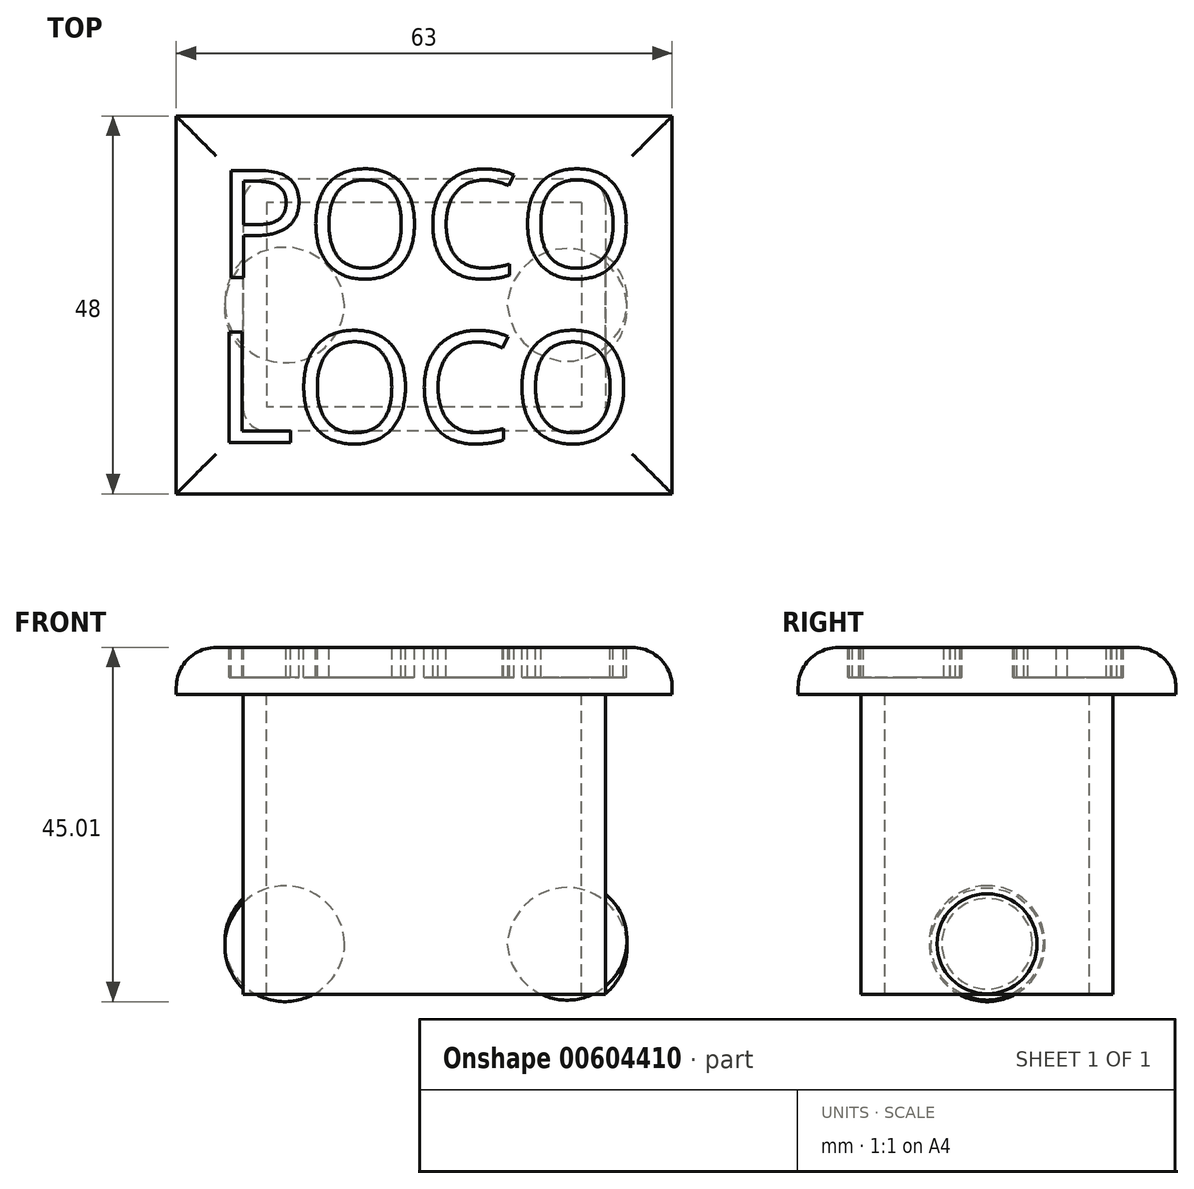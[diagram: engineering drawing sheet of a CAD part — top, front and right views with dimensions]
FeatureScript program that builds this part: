
annotation { "Feature Type Name" : "Feature", "Feature Type Description" : "" }
export const myFeature = defineFeature(function(context is Context, id is Id, definition is map)
    precondition{}
    {
        {
            var Q0;
            Q0=qCreatedBy(makeId("Top.planeOp"),FACE);
            var sketch = newSketch(context, id + "F0", { "sketchPlane" : qUnion([Q0])});
            skLineSegment(sketch, "E0.bottom", {"start": v(31.5, -24) * mm, "end": v(-31.5, -24) * mm});
            skLineSegment(sketch, "E0.top", {"start": v(31.5, 24) * mm, "end": v(-31.5, 24) * mm});
            skLineSegment(sketch, "E0.left", {"start": v(31.5, -24) * mm, "end": v(31.5, 24) * mm});
            skLineSegment(sketch, "E0.right", {"start": v(-31.5, -24) * mm, "end": v(-31.5, 24) * mm});
            skPoint(sketch, "E0.middle", {"position": v(0, 0) * mm});
            skSolve(sketch);
        }
        {
            var Q0;
            Q0=makeQuery(id+"F0.imprint","IMPRINT",FACE,{"disambiguationData":[TD([[makeQuery(id+"F0.imprint","IMPRINT",EDGE,{"derivedFrom":sQuery(id+"F0.wireOp",EDGE,"E0.bottom")}),-1.0]])]});
            extrude(context, id + "F1", {"entities" : qUnion([Q0]), "depth" : 6 * mm, "offsetDistance" : 25.4 * mm});
        }
        {
            var Q0;
            Q0=makeQuery(id+"F1.opExtrude","CAP_FACE",FACE,{"disambiguationData":[OSD([sQuery(id+"F0.wireOp",EDGE,"E0.bottom"),sQuery(id+"F0.wireOp",EDGE,"E0.top"),sQuery(id+"F0.wireOp",EDGE,"E0.left"),sQuery(id+"F0.wireOp",EDGE,"E0.right")])],"isStart":true});
            var sketch = newSketch(context, id + "F2", { "sketchPlane" : qUnion([Q0])});
            skLineSegment(sketch, "E1.bottom", {"start": v(20, -16) * mm, "end": v(-20, -16) * mm});
            skLineSegment(sketch, "E1.top", {"start": v(20, 16) * mm, "end": v(-20, 16) * mm});
            skLineSegment(sketch, "E1.left", {"start": v(23, -13) * mm, "end": v(23, -6.14) * mm});
            skLineSegment(sketch, "E1.right", {"start": v(-23, -13) * mm, "end": v(-23, -5.27) * mm});
            skPoint(sketch, "E1.middle", {"position": v(0, 0) * mm});
            skLineSegment(sketch, "E2.bottom", {"start": v(20, -13) * mm, "end": v(-20, -13) * mm});
            skLineSegment(sketch, "E2.top", {"start": v(20, 13) * mm, "end": v(-20, 13) * mm});
            skLineSegment(sketch, "E2.left", {"start": v(20, -13) * mm, "end": v(20, -6.14) * mm});
            skLineSegment(sketch, "E2.right", {"start": v(-20, -13) * mm, "end": v(-20, -5.27) * mm});
            skPoint(sketch, "E3.visualSharp", {"position": v(-23, 16) * mm});
            skArc(sketch, "E3.filletArc", {"start": v(-20, 16) * mm, "mid": v(-22.12, 15.12) * mm, "end": v(-23, 13) * mm});
            skPoint(sketch, "E4.visualSharp", {"position": v(23, 16) * mm});
            skArc(sketch, "E4.filletArc", {"start": v(23, 13) * mm, "mid": v(22.12, 15.12) * mm, "end": v(20, 16) * mm});
            skPoint(sketch, "E5.visualSharp", {"position": v(23, -16) * mm});
            skArc(sketch, "E5.filletArc", {"start": v(20, -16) * mm, "mid": v(22.12, -15.12) * mm, "end": v(23, -13) * mm});
            skPoint(sketch, "E6.visualSharp", {"position": v(-23, -16) * mm});
            skArc(sketch, "E6.filletArc", {"start": v(-23, -13) * mm, "mid": v(-22.12, -15.12) * mm, "end": v(-20, -16) * mm});
            skLineSegment(sketch, "E7.trimOffspring", {"start": v(-23, -4.17) * mm, "end": v(-23, 4.46) * mm});
            skLineSegment(sketch, "E8.trimOffspring", {"start": v(-20, -4.17) * mm, "end": v(-20, 4.46) * mm});
            skLineSegment(sketch, "E9.trimOffspring", {"start": v(-20, 5.41) * mm, "end": v(-20, 13) * mm});
            skLineSegment(sketch, "E10.trimOffspring", {"start": v(-23, 5.41) * mm, "end": v(-23, 13) * mm});
            skLineSegment(sketch, "E11.trimOffspring", {"start": v(20, 5.32) * mm, "end": v(20, 13) * mm});
            skLineSegment(sketch, "E12.trimOffspring", {"start": v(23, 5.32) * mm, "end": v(23, 13) * mm});
            skLineSegment(sketch, "E13.trimOffspring", {"start": v(20, -4.92) * mm, "end": v(20, 4.27) * mm});
            skLineSegment(sketch, "E14", {"start": v(23, 4.27) * mm, "end": v(23, -4.92) * mm});
            skLineSegment(sketch, "E15", {"start": v(-23, 5.41) * mm, "end": v(-23, 4.46) * mm});
            skLineSegment(sketch, "E16", {"start": v(-23, -5.27) * mm, "end": v(-23, -4.17) * mm});
            skLineSegment(sketch, "E17", {"start": v(-20, -4.17) * mm, "end": v(-20, -5.27) * mm});
            skLineSegment(sketch, "E18", {"start": v(-20, 4.46) * mm, "end": v(-20, 5.41) * mm});
            skLineSegment(sketch, "E19", {"start": v(20, 5.32) * mm, "end": v(20, 4.27) * mm});
            skLineSegment(sketch, "E20", {"start": v(20, -4.92) * mm, "end": v(20, -6.14) * mm});
            skLineSegment(sketch, "E21", {"start": v(23, -6.14) * mm, "end": v(23, -4.92) * mm});
            skLineSegment(sketch, "E22", {"start": v(23, 5.32) * mm, "end": v(23, 4.27) * mm});
            skSolve(sketch);
        }
        {
            var Q0;
            Q0=makeQuery(id+"F2.imprint","IMPRINT",FACE,{"disambiguationData":[TD([[makeQuery(id+"F2.imprint","IMPRINT",EDGE,{"derivedFrom":sQuery(id+"F2.wireOp",EDGE,"E1.bottom")}),-1.0]])]});
            extrude(context, id + "F3", {"entities" : qUnion([Q0]), "operationType" : NewBodyOperationType.ADD, "depth" : 38.1 * mm, "offsetDistance" : 25.4 * mm});
        }
        {
            var Q0;
            Q0=makeQuery(id+"F1.opExtrude","CAP_EDGE",EDGE,{"disambiguationData":[OSD([sQuery(id+"F0.wireOp",EDGE,"E0.right")])],"isStart":false});
            var Q1;
            Q1=makeQuery(id+"F1.opExtrude","CAP_EDGE",EDGE,{"disambiguationData":[OSD([sQuery(id+"F0.wireOp",EDGE,"E0.top")])],"isStart":false});
            var Q2;
            Q2=makeQuery(id+"F1.opExtrude","CAP_EDGE",EDGE,{"disambiguationData":[OSD([sQuery(id+"F0.wireOp",EDGE,"E0.left")])],"isStart":false});
            var Q3;
            Q3=makeQuery(id+"F1.opExtrude","CAP_EDGE",EDGE,{"disambiguationData":[OSD([sQuery(id+"F0.wireOp",EDGE,"E0.bottom")])],"isStart":false});
            fillet(context, id + "F4", {"entities" : qUnion([Q0, Q1, Q2, Q3]), "radius" : 5.08 * mm, "tangentPropagation" : true, "allowEdgeOverflow" : false});
        }
        {
            var Q0;
            Q0=makeQuery(id+"F1.opExtrude","CAP_FACE",FACE,{"disambiguationData":[OSD([sQuery(id+"F0.wireOp",EDGE,"E0.bottom"),sQuery(id+"F0.wireOp",EDGE,"E0.top"),sQuery(id+"F0.wireOp",EDGE,"E0.left"),sQuery(id+"F0.wireOp",EDGE,"E0.right")])],"isStart":false});
            var sketch = newSketch(context, id + "F5", { "sketchPlane" : qUnion([Q0])});
            skText(sketch, "E23", { "text": "POCO", "fontName": "OpenSans-Regular.ttf"});
            skText(sketch, "E24", { "text": "LOCO", "fontName": "OpenSans-Regular.ttf"});
            const initialGuessF5  = {"E23": [-0.02642, 0.00346, 1, 0, 0.01374], "E24": [-0.02671, -0.01748, 1, 0, 0.01416]};
            skSetInitialGuess(sketch, initialGuessF5);
            skSolve(sketch);
        }
        {
            var Q0;
            Q0 = qSketchRegion(id + "F5", true);
            extrude(context, id + "F6", {"entities" : qUnion([Q0]), "operationType" : NewBodyOperationType.REMOVE, "oppositeDirection" : true, "depth" : 3.8 * mm, "offsetDistance" : 25.4 * mm});
        }
        {
            var Q0;
            Q0 = qSketchRegion(id + "F2", true);
            extrude(context, id + "F7", {"entities" : qUnion([Q0]), "operationType" : NewBodyOperationType.ADD, "depth" : 25.4 * mm, "offsetDistance" : 25.4 * mm});
        }
        {
            var Q0;
            Q0=qCreatedBy(makeId("Front.planeOp"),FACE);
            var sketch = newSketch(context, id + "F8", { "sketchPlane" : qUnion([Q0])});
            skLineSegment(sketch, "E25", {"start": v(-23, -37.4) * mm, "end": v(-23, -31.65) * mm});
            skLineSegment(sketch, "E26", {"start": v(-23, -31.65) * mm, "end": v(-25.32, -31.65) * mm});
            skArc(sketch, "E27", {"start": v(-25.32, -31.65) * mm, "mid": v(-24.77, -34.77) * mm, "end": v(-23, -37.4) * mm});
            skSolve(sketch);
        }
        {
            var Q0;
            Q0=makeQuery(id+"F8.imprint","IMPRINT",FACE,{"disambiguationData":[TD([[makeQuery(id+"F8.imprint","IMPRINT",EDGE,{"derivedFrom":sQuery(id+"F8.wireOp",EDGE,"E25")}),1.0]])]});
            var Q1;
            Q1 = qSketchRegion(id + "F8", true);
            var Q2;
            Q2=sQuery(id+"F8.wireOp",EDGE,"E26");
            revolve(context, id + "F9", {"operationType" : NewBodyOperationType.ADD, "entities" : qUnion([Q0, Q1]), "axis" : qUnion([Q2]), "revolveType" : RevolveType.FULL});
        }
        {
            var Q0;
            Q0=qCreatedBy(makeId("Front.planeOp"),FACE);
            var sketch = newSketch(context, id + "F10", { "sketchPlane" : qUnion([Q0])});
            skLineSegment(sketch, "E28", {"start": v(23, -38.02) * mm, "end": v(23, -31.67) * mm});
            skLineSegment(sketch, "E29", {"start": v(23, -31.67) * mm, "end": v(25.76, -31.67) * mm});
            skArc(sketch, "E30", {"start": v(23, -38.02) * mm, "mid": v(25.14, -35.17) * mm, "end": v(25.76, -31.67) * mm});
            skSolve(sketch);
        }
        {
            var Q0;
            Q0=makeQuery(id+"F10.imprint","IMPRINT",FACE,{"disambiguationData":[TD([[makeQuery(id+"F10.imprint","IMPRINT",EDGE,{"derivedFrom":sQuery(id+"F10.wireOp",EDGE,"E28")}),-1.0]])]});
            var Q1;
            Q1=sQuery(id+"F10.wireOp",EDGE,"E29");
            revolve(context, id + "F11", {"operationType" : NewBodyOperationType.ADD, "entities" : qUnion([Q0]), "axis" : qUnion([Q1]), "revolveType" : RevolveType.FULL});
        }
    });
